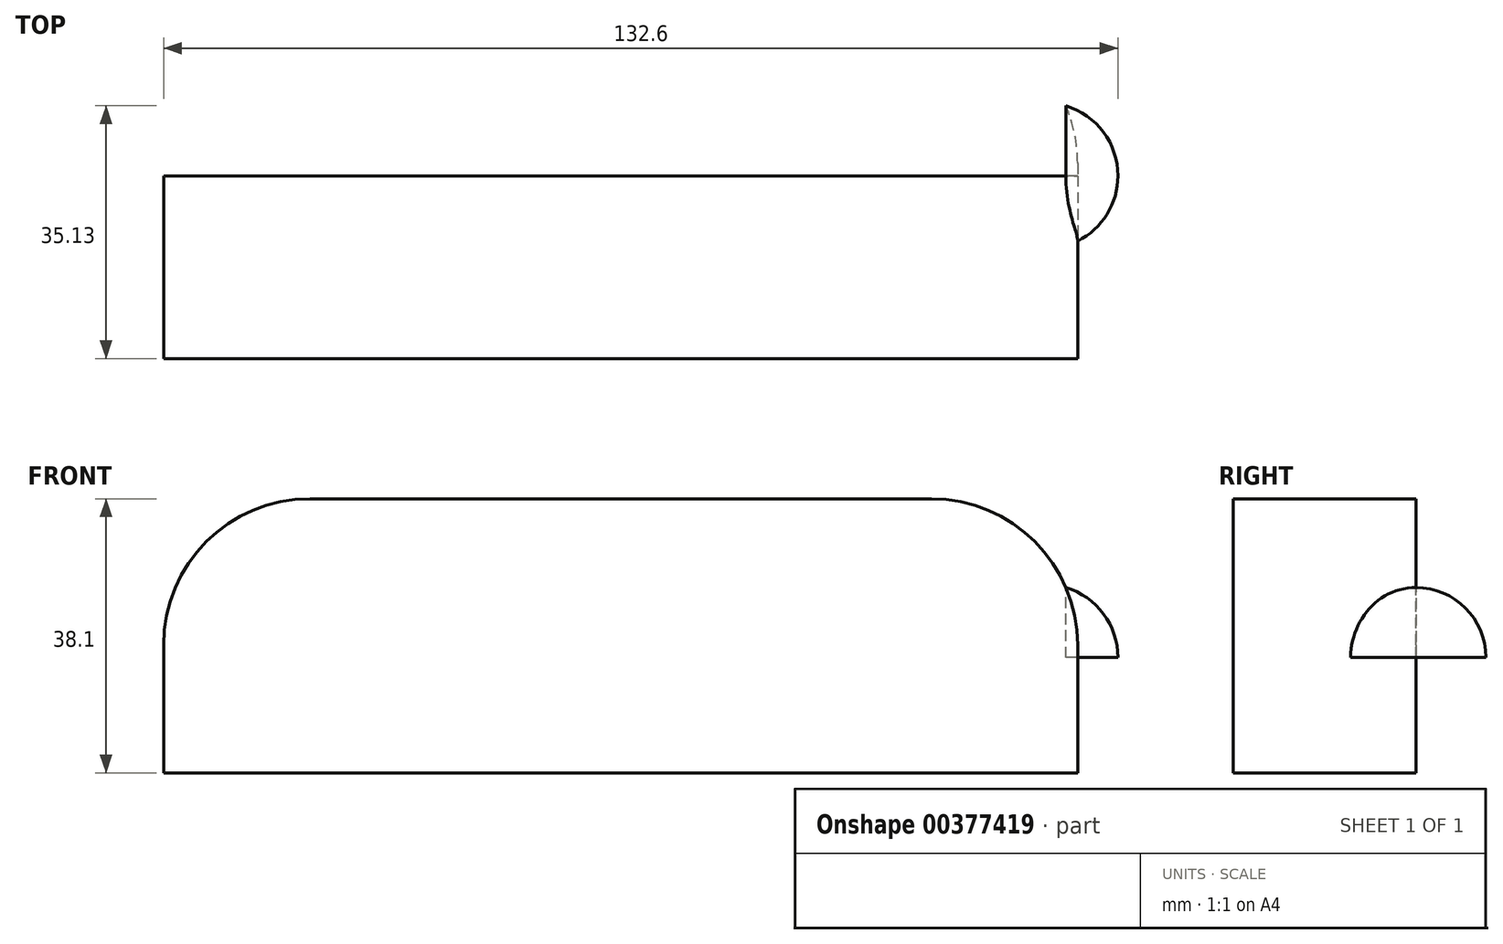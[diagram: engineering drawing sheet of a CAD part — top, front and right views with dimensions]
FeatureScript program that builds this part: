
annotation { "Feature Type Name" : "Feature", "Feature Type Description" : "" }
export const myFeature = defineFeature(function(context is Context, id is Id, definition is map)
    precondition{}
    {
        {
            var Q0;
            Q0=qCreatedBy(makeId("Front.planeOp"),FACE);
            var sketch = newSketch(context, id + "F0", { "sketchPlane" : qUnion([Q0])});
            skLineSegment(sketch, "E0.bottom", {"start": v(91.2, 38.1) * mm, "end": v(4.84, 38.1) * mm});
            skLineSegment(sketch, "E0.top", {"start": v(111.52, 0) * mm, "end": v(-15.48, 0) * mm});
            skLineSegment(sketch, "E0.left", {"start": v(111.52, 17.78) * mm, "end": v(111.52, 0) * mm});
            skLineSegment(sketch, "E0.right", {"start": v(-15.48, 17.78) * mm, "end": v(-15.48, 0) * mm});
            skLineSegment(sketch, "E1.bottom", {"start": v(4.84, 38.1) * mm, "end": v(91.2, 38.1) * mm});
            skLineSegment(sketch, "E1.top", {"start": v(23.89, 57.15) * mm, "end": v(72.15, 57.15) * mm});
            skLineSegment(sketch, "E1.left", {"start": v(4.84, 38.1) * mm, "end": v(4.84, 38.1) * mm});
            skLineSegment(sketch, "E1.right", {"start": v(91.2, 38.1) * mm, "end": v(91.2, 38.1) * mm});
            skPoint(sketch, "E2.visualSharp", {"position": v(111.52, 38.1) * mm});
            skArc(sketch, "E2.filletArc", {"start": v(111.52, 17.78) * mm, "mid": v(105.57, 32.15) * mm, "end": v(91.2, 38.1) * mm});
            skPoint(sketch, "E3.visualSharp", {"position": v(-15.48, 38.1) * mm});
            skArc(sketch, "E3.filletArc", {"start": v(4.84, 38.1) * mm, "mid": v(-9.53, 32.15) * mm, "end": v(-15.48, 17.78) * mm});
            skPoint(sketch, "E4.visualSharp", {"position": v(91.2, 57.15) * mm});
            skArc(sketch, "E4.filletArc", {"start": v(91.2, 38.1) * mm, "mid": v(85.62, 51.57) * mm, "end": v(72.15, 57.15) * mm});
            skPoint(sketch, "E5.visualSharp", {"position": v(4.84, 57.15) * mm});
            skArc(sketch, "E5.filletArc", {"start": v(23.89, 57.15) * mm, "mid": v(10.42, 51.57) * mm, "end": v(4.84, 38.1) * mm});
            skLineSegment(sketch, "E6", {"start": v(-15.48, 2.54) * mm, "end": v(-21.09, 2.54) * mm});
            skLineSegment(sketch, "E7", {"start": v(-21.09, 2.54) * mm, "end": v(-21.09, 16.04) * mm});
            skPoint(sketch, "E8.visualSharp", {"position": v(-21.09, 16.04) * mm});
            skArc(sketch, "E8.filletArc", {"start": v(-13.85, 25.77) * mm, "mid": v(-19.08, 22.1) * mm, "end": v(-21.09, 16.04) * mm});
            skPoint(sketch, "E9.orphan", {"position": v(-15.48, 25.79) * mm});
            skLineSegment(sketch, "E10", {"start": v(111.52, 2.54) * mm, "end": v(117.12, 2.54) * mm});
            skLineSegment(sketch, "E11", {"start": v(117.12, 2.54) * mm, "end": v(117.12, 16.04) * mm});
            skPoint(sketch, "E12.visualSharp", {"position": v(117.12, 25.79) * mm});
            skArc(sketch, "E12.filletArc", {"start": v(117.12, 16.04) * mm, "mid": v(115.12, 22.1) * mm, "end": v(109.88, 25.77) * mm});
            skLineSegment(sketch, "E13", {"start": v(117.12, 16.04) * mm, "end": v(111.52, 16.04) * mm});
            skLineSegment(sketch, "E14", {"start": v(-21.09, 16.04) * mm, "end": v(-15.48, 16.04) * mm});
            skSolve(sketch);
        }
        {
            var Q0;
            Q0=qCreatedBy(makeId("Front.planeOp"),FACE);
            cPlane(context, id + "F1", {"entities" : qUnion([Q0]), "cplaneType" : CPlaneType.OFFSET, "offset" : 25.4 * mm, "width" : 152.4 * mm, "height" : 152.4 * mm});
        }
        {
            var Q0;
            Q0=qCreatedBy(id+"F1.planeOp",FACE);
            var sketch = newSketch(context, id + "F2", { "sketchPlane" : qUnion([Q0])});
            skArc(sketch, "E15.0.0", {"start": v(111.52, 17.78) * mm, "mid": v(111.1, 21.86) * mm, "end": v(109.88, 25.77) * mm});
            skArc(sketch, "E15.0.1", {"start": v(109.88, 25.77) * mm, "mid": v(102.4, 34.74) * mm, "end": v(91.2, 38.1) * mm});
            skLineSegment(sketch, "E15.0.2", {"start": v(91.2, 38.1) * mm, "end": v(4.84, 38.1) * mm});
            skArc(sketch, "E15.0.3", {"start": v(4.84, 38.1) * mm, "mid": v(-6.36, 34.74) * mm, "end": v(-13.85, 25.77) * mm});
            skArc(sketch, "E15.0.4", {"start": v(-13.85, 25.77) * mm, "mid": v(-15.07, 21.86) * mm, "end": v(-15.48, 17.78) * mm});
            skLineSegment(sketch, "E15.0.5", {"start": v(-15.48, 17.78) * mm, "end": v(-15.48, 16.04) * mm});
            skLineSegment(sketch, "E15.0.6", {"start": v(-15.48, 16.04) * mm, "end": v(-15.48, 0) * mm});
            skLineSegment(sketch, "E15.0.7", {"start": v(-15.48, 0) * mm, "end": v(111.52, 0) * mm});
            skLineSegment(sketch, "E15.0.8", {"start": v(111.52, 0) * mm, "end": v(111.52, 2.54) * mm});
            skLineSegment(sketch, "E15.0.9", {"start": v(111.52, 2.54) * mm, "end": v(111.52, 17.78) * mm});
            skSolve(sketch);
        }
        {
            var Q0;
            Q0=makeQuery(id+"F2.imprint","IMPRINT",FACE,{"disambiguationData":[TD([[makeQuery(id+"F2.imprint","IMPRINT",EDGE,{"derivedFrom":sQuery(id+"F2.wireOp",EDGE,"E15.0.0")}),1.0]])]});
            extrude(context, id + "F3", {"entities" : qUnion([Q0]), "oppositeDirection" : true, "depth" : 25.4 * mm});
        }
        {
            var Q0;
            {var subQ4=sQuery(id+"F0.wireOp",EDGE,"E12.filletArc");Q0=makeQuery(id+"F0.imprint","IMPRINT",FACE,{"disambiguationData":[TD([[makeQuery(id+"F0.imprint","IMPRINT",EDGE,{"derivedFrom":subQ4}),1.0]])]});}
            var Q1;
            Q1=sQuery(id+"F0.wireOp",EDGE,"E13");
            revolve(context, id + "F4", {"operationType" : NewBodyOperationType.ADD, "entities" : qUnion([Q0]), "axis" : qUnion([Q1]), "revolveType" : RevolveType.TWO_DIRECTIONS, "angle" : 90 * degree, "angleBack" : 270 * degree});
        }
    });
